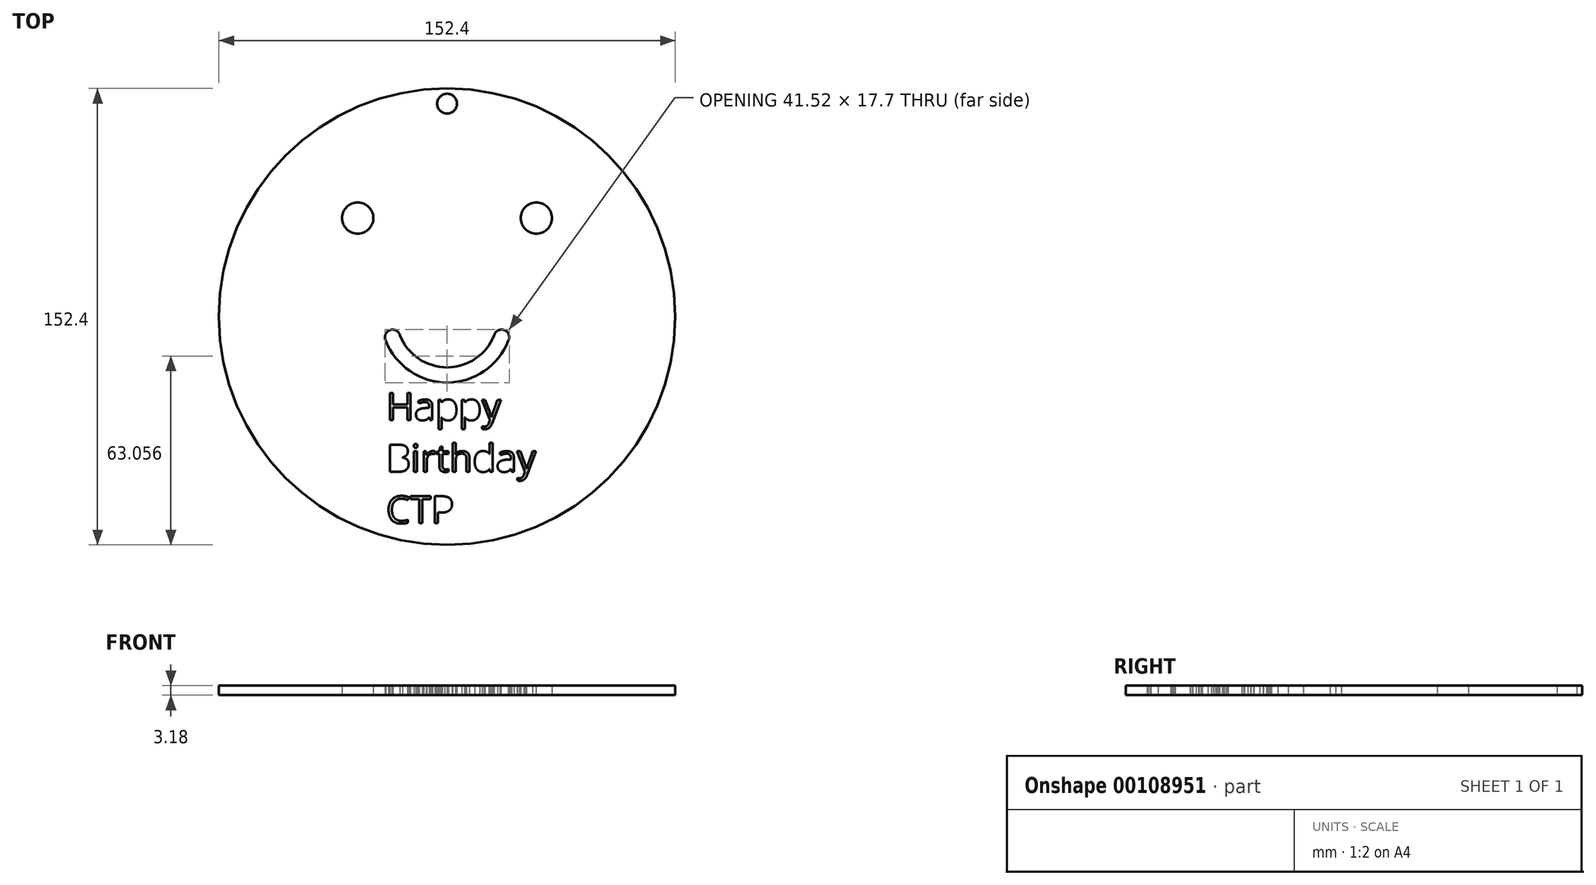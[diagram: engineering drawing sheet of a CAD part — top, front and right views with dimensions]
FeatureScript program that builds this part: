
annotation { "Feature Type Name" : "Feature", "Feature Type Description" : "" }
export const myFeature = defineFeature(function(context is Context, id is Id, definition is map)
    precondition{}
    {
        {
            var Q0;
            Q0=qCreatedBy(makeId("Top.planeOp"),FACE);
            var sketch = newSketch(context, id + "F0", { "sketchPlane" : qUnion([Q0])});
            skCircle(sketch, "E0", {"center": v(0, 0) * mm, "radius": 76.2 * mm});
            skCircle(sketch, "E1", {"center": v(-29.84, 32.95) * mm, "radius": 5.22 * mm});
            skCircle(sketch, "E2.MirrorC", {"center": v(29.84, 32.95) * mm, "radius": 5.22 * mm});
            skArc(sketch, "E3", {"start": v(-20.48, -8.01) * mm, "mid": v(-12.4, -18.16) * mm, "end": v(0, -22) * mm});
            skArc(sketch, "E4.0", {"start": v(-15.75, -6.16) * mm, "mid": v(-9.53, -13.97) * mm, "end": v(0, -16.91) * mm});
            skArc(sketch, "E5", {"start": v(-15.75, -6.16) * mm, "mid": v(-19.14, -4.47) * mm, "end": v(-20.48, -8.01) * mm});
            skArc(sketch, "E6.MirrorCS", {"start": v(15.75, -6.16) * mm, "mid": v(9.53, -13.97) * mm, "end": v(0, -16.91) * mm});
            skArc(sketch, "E7.MirrorCS", {"start": v(20.48, -8.01) * mm, "mid": v(12.4, -18.16) * mm, "end": v(0, -22) * mm});
            skArc(sketch, "E8.MirrorCS", {"start": v(15.75, -6.16) * mm, "mid": v(19.14, -4.47) * mm, "end": v(20.48, -8.01) * mm});
            skCircle(sketch, "E9", {"center": v(0, 71.12) * mm, "radius": 3.3 * mm});
            skText(sketch, "E10", { "text": "Happy\nBirthday\nCTP", "fontName": "OpenSans-Regular.ttf"});
            const initialGuessF0  = {"E10": [-0.02032, -0.03452, 1, 0, 0.00912]};
            skSetInitialGuess(sketch, initialGuessF0);
            skSolve(sketch);
        }
        {
            var Q0;
            Q0=makeQuery(id+"F0.imprint","IMPRINT",FACE,{"disambiguationData":[TD([[makeQuery(id+"F0.imprint","IMPRINT",EDGE,{"derivedFrom":sQuery(id+"F0.wireOp",EDGE,"E0")}),1.0]])]});
            extrude(context, id + "F1", {"entities" : qUnion([Q0]), "depth" : 3.17 * mm});
        }
    });
